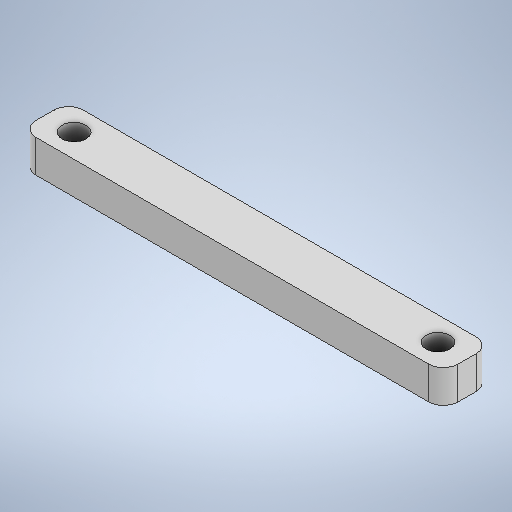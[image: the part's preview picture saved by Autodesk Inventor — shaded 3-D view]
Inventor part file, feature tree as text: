
AUTODESK INVENTOR PART (.ipt)
format: ipt  version: 2025.1 (Build 291241020, 241B)  size: 719,872 bytes
history: native  units: in
note: dims shown in document units (in); Inventor stores cm internally (conversion verified against a paired STEP export)
features: extrude x15, sketch x15, other x3, fillet x3, pattern_circular x1
ambient origin geometry x8: Origin, YZ Plane, XZ Plane, XY Plane, X Axis, Y Axis, Z Axis, Center Point
bodies: Solid1 (feature_tree)
feature tree (37):
  other  "servoMoldAssembly.iam"
  other  "block.ipt:1"
  other  "sg90horn.ipt:1"
  extrude  "Extrusion1"  Depth=0.3937in TaperAngle=0.0deg
  extrude  "Extrusion2"  Depth=0.3937in TaperAngle=0.0deg
  extrude  "Extrusion3"  Depth=0.0591in TaperAngle=0.0deg
  extrude  "Extrusion4"  Depth=0.0591in TaperAngle=0.0deg
  extrude  "Extrusion5"  Depth=1.9685in
  extrude  "Extrusion6"  Depth=0.3937in TaperAngle=0.0deg
  extrude  "Extrusion7"  Depth=0.3937in TaperAngle=0.0deg
  extrude  "Extrusion8"  Depth=0.1299in
  extrude  "Extrusion10"  Depth=0.0787in TaperAngle=0.0deg
  extrude  "Extrusion11"  Depth=0.0787in TaperAngle=0.0deg
  fillet  "Fillet1"  Radius=0.0787in
  extrude  "Extrusion12"  Depth=0.8268in
  fillet  "Fillet2"  Radius=1.1934in
  extrude  "Extrusion13"  TaperAngle=90.0deg  [1 undecoded]
  pattern_circular  "Circular Pattern2"  Count=20 Angle=240.0deg
  extrude  "Extrusion14"  Depth=0.3937in
  extrude  "Extrusion15"  Depth=0.0787in
  extrude  "Extrusion16"  Depth=0.3937in TaperAngle=0.0deg
  fillet  "Fillet3"  Radius=0.0787in
  sketch  "Sketch3"  dims[d0=0.3937in d1=0.3937in d2=0.0in]
  sketch  "Sketch4"  dims[d3=0.2795in d4=0.3937in d5=0.0in]
  sketch  "Sketch5"  dims[d6=0.0591in d7=0.0in d8=0.0591in d9=0.0in]
  sketch  "Sketch6"  dims[d10=0.0591in d11=0.0in d12=0.0591in d13=0.0in]
  sketch  "Sketch7"  dims[d14=1.4173in d15=1.9685in]
  sketch  "Sketch8"  dims[d16=0.0in d17=0.3937in d18=0.0in]
  sketch  "Sketch9"  dims[d19=0.3937in d20=0.0in d29=0.2362in d30=0.0in]
  sketch  "Sketch10"  dims[d31=0.2362in d32=0.1299in]
  sketch  "Sketch12"  dims[d33=0.0787in d34=0.2362in d35=0.0in]
  sketch  "Sketch13"  dims[d36=0.0787in d37=0.2362in d38=0.0in d39=0.0787in]
  sketch  "Sketch14"  dims[d40=0.0984in d41=0.8268in d42=1.1934in]
  sketch  "Sketch15"  dims[d43=0.0591in d44=90.0deg]
  sketch  "Sketch16"  dims[d45=0.3937in d46=0.0in d47=7.874in d48=240.0deg]
  sketch  "Sketch17"  dims[d50=0.3937in d51=0.0in d52=0.1299in]
  sketch  "Sketch18"  dims[d53=0.3937in d54=0.0in d55=0.1575in d56=0.3937in d57=0.0in d58=0.0787in]
note: 1 required parameter value undecoded (feature->parameter linkage not recoverable at this tier; creation-order binding heuristic only, values carry confidence <= 0.55)
